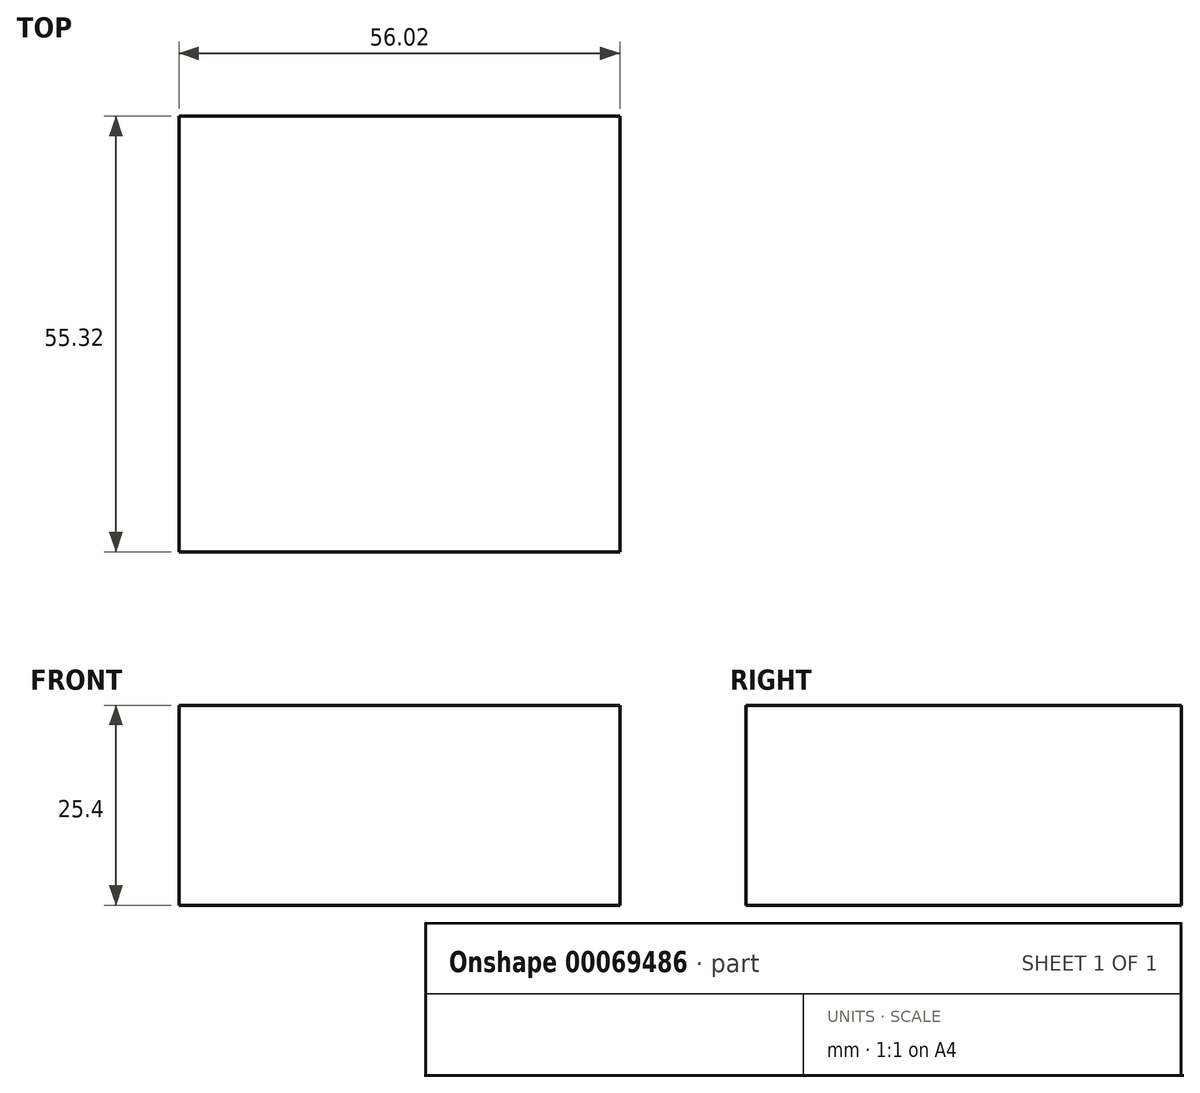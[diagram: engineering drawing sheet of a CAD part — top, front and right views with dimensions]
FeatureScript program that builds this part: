
annotation { "Feature Type Name" : "Feature", "Feature Type Description" : "" }
export const myFeature = defineFeature(function(context is Context, id is Id, definition is map)
    precondition{}
    {
        {
            var Q0;
            Q0=qCreatedBy(makeId("Top.planeOp"),FACE);
            var sketch = newSketch(context, id + "F0", { "sketchPlane" : qUnion([Q0])});
            skLineSegment(sketch, "E0.rect.bottom", {"start": v(-28, 27.66) * mm, "end": v(28, 27.66) * mm});
            skLineSegment(sketch, "E0.rect.top", {"start": v(-28, -27.66) * mm, "end": v(28, -27.66) * mm});
            skLineSegment(sketch, "E0.rect.left", {"start": v(-28, 27.66) * mm, "end": v(-28, -27.66) * mm});
            skLineSegment(sketch, "E0.rect.right", {"start": v(28, 27.66) * mm, "end": v(28, -27.66) * mm});
            skPoint(sketch, "E0.rect.middle", {"position": v(0, 0) * mm});
            skSolve(sketch);
        }
        {
            var Q0;
            Q0 = qSketchRegion(id + "F0", true);
            extrude(context, id + "F1", {"entities" : qUnion([Q0]), "depth" : 25.4 * mm});
        }
    });
